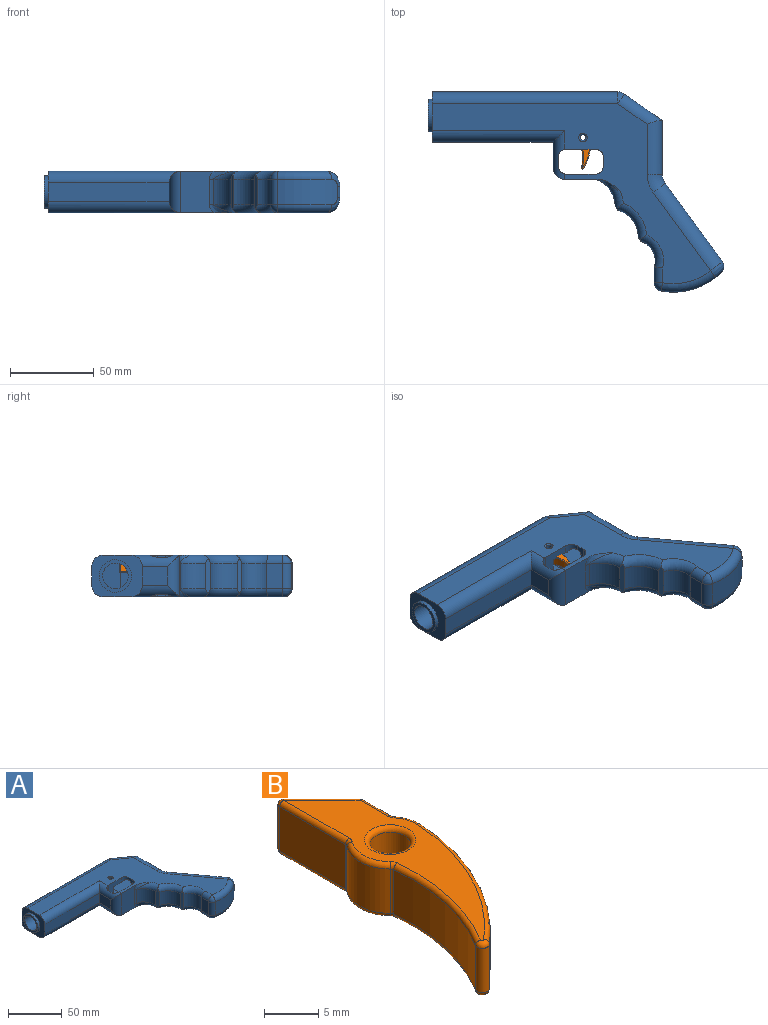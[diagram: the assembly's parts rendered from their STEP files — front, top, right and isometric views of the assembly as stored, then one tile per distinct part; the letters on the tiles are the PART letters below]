
ASSEMBLY  parts=2 mates=1
PART A: 95 faces, bbox 178.8x123.7x40 mm
  f0: plane 15.06x11mm, normal (-1,0,0), area 165.6mm2, adj f72,f87,f88,f89
  f1: cylinder r=5mm len=5mm, axis (0,0,-1), area 29.1mm2, adj f2,f6,f18,f44,f50,f52
  f2: plane 25x17mm, normal (0,-1,0), area 268.3mm2, adj f1,f3,f17,f18,f43,f44,f45,f65
  f3: cylinder r=5mm len=5mm, axis (0,0,-1), area 29.2mm2, adj f2,f6,f17,f45,f51,f53
  f4: cylinder r=40.62mm len=35.92mm, axis (0,0,-1), area 568.7mm2, adj f25,f28,f29,f33,f34,f42
  f5: plane 22.49x5mm, normal (1,0,0), area 112.4mm2, adj f65,f66,f87,f89
  f6: plane 25x5mm, normal (-1,0,0), area 69.7mm2, adj f1,f3,f17,f18,f19,f52,f53,f55
  f7: plane 25.01x19.08mm, normal (0,-1,0), area 427.6mm2, adj f17,f18,f76,f77,f78,f88
  f8: cylinder r=17mm len=15.25mm, axis (0,0,-1), area 292.7mm2, adj f9,f20,f21,f77
  f9: plane 21.32x3.15mm, normal (-0.86,-0.52,0), area 56.6mm2, adj f8,f10,f20,f21,f22,f23
  f10: cylinder r=17mm len=16.26mm, axis (0,0,-1), area 328mm2, adj f9,f11,f22,f23
  f11: plane 21.33x2.99mm, normal (-0.82,-0.57,0), area 56.7mm2, adj f10,f12,f22,f23,f24,f26
  f12: cylinder r=12mm len=15.05mm, axis (0,0,-1), area 282.2mm2, adj f11,f13,f24,f26
  f13: plane 15x9.54mm, normal (-1,0,0), area 143.2mm2, adj f12,f27,f30,f33
  f14: plane 46.5x34.02mm, normal (0.81,0.59,0), area 403.3mm2, adj f25,f35,f38,f41
  f15: plane 32.06x7mm, normal (1,0,0), area 224.4mm2, adj f36,f38,f39,f73
  f16: plane 25x17mm, normal (0,1,0), area 425mm2, adj f17,f18,f19,f66
  f17: plane 165.74x107.32mm, normal (0,0,1), area 4323.9mm2, adj f2,f3,f6,f7,f16,f19,f20,f22
  f18: plane 165.74x107.32mm, normal (0,0,-1), area 4323.9mm2, adj f1,f2,f6,f7,f16,f19,f21,f23
  f19: cylinder r=5mm len=25mm, axis (0,0,1), area 196.3mm2, adj f6,f16,f17,f18
  f20: torus R=22mm, axis (0,0,1), area 115.2mm2, adj f8,f9,f17,f22,f78
  f21: torus R=22mm, axis (0,0,1), area 115.2mm2, adj f8,f9,f18,f23,f76
  f22: torus R=22mm, axis (0,0,1), area 190.9mm2, adj f9,f10,f11,f17,f20,f24
  f23: torus R=22mm, axis (0,0,1), area 190.9mm2, adj f9,f10,f11,f18,f21,f26
  f24: torus R=17mm, axis (0,0,1), area 168mm2, adj f11,f12,f17,f22,f27
  f25: cylinder r=5mm len=7mm, axis (0,0,-1), area 49.6mm2, adj f4,f14,f34,f42
  f26: torus R=17mm, axis (0,0,1), area 168mm2, adj f11,f12,f18,f23,f30
  f27: cylinder r=5mm len=9.54mm, axis (0,1,0), area 72.2mm2, adj f13,f17,f24,f31
  f28: torus R=35.62mm, axis (0,0,1), area 259.2mm2, adj f4,f17,f31,f34
  f29: torus R=35.62mm, axis (0,0,1), area 259.2mm2, adj f4,f18,f32,f42
  f30: cylinder r=5mm len=9.54mm, axis (0,-1,0), area 72.2mm2, adj f13,f18,f26,f32
  f31: sphere r=5mm, area 34.8mm2, adj f27,f28,f33
  f32: sphere r=5mm, area 34.8mm2, adj f29,f30,f33
  f33: cylinder r=5mm len=15mm, axis (0,0,-1), area 104.4mm2, adj f4,f13,f31,f32
  f34: bspline ~10.77x10.52mm, area 85.1mm2, adj f4,f25,f28,f35
  f35: cylinder r=9mm len=52.13mm, axis (0.59,-0.81,0), area 817.3mm2, adj f14,f17,f34,f37
  f36: cylinder r=9mm len=32.06mm, axis (0,-1,0), area 445.2mm2, adj f15,f17,f37,f70,f79
  f37: torus R=18mm, axis (0,0,1), area 109.6mm2, adj f17,f35,f36,f38
  f38: cylinder r=9mm len=7mm, axis (0,0,1), area 39.8mm2, adj f14,f15,f37,f40
  f39: cylinder r=9mm len=32.06mm, axis (0,1,0), area 445.2mm2, adj f15,f18,f40,f71,f82
  f40: torus R=18mm, axis (0,0,1), area 109.6mm2, adj f18,f38,f39,f41
  f41: cylinder r=9mm len=52.13mm, axis (-0.59,0.81,0), area 817.3mm2, adj f14,f18,f40,f42
  f42: bspline ~10.63x10.55mm, area 85.1mm2, adj f4,f25,f29,f41
  f43: plane 15x4mm, normal (1,0,0), area 60mm2, adj f2,f44,f45,f58
  f44: plane 17.55x16.25mm, normal (0,0,1), area 233.8mm2, adj f1,f2,f43,f48,f49,f50,f58,f59
  f45: plane 17.63x16.27mm, normal (0,0,-1), area 235mm2, adj f2,f3,f43,f48,f49,f51,f58,f60
  f46: cylinder r=1.75mm len=3.5mm, axis (0,0,1), area 38.5mm2, adj f63,f64
  f47: cylinder r=1.75mm len=3.5mm, axis (0,0,1), area 38.5mm2, adj f61,f62
  f48: plane 17x12mm, normal (1,0,0), area 133.9mm2, adj f44,f45,f49,f59,f60,f69,f91
  f49: plane 15x4.55mm, normal (0,1,0), area 68.3mm2, adj f44,f45,f48,f58
  f50: plane 18.9x2.42mm, normal (0.71,0,0.71), area 49.9mm2, adj f1,f44,f52,f59,f69
  f51: plane 18.89x2.41mm, normal (0.72,0,-0.69), area 49.1mm2, adj f3,f45,f53,f60,f69
  f52: plane 27.45x23mm, normal (0,0,1), area 626.3mm2, adj f1,f6,f50,f56,f68,f69
  f53: plane 27.45x23mm, normal (0,0,-1), area 626.3mm2, adj f3,f6,f51,f57,f67,f69
  f54: plane 25x15mm, normal (-1,0,0), area 375mm2, adj f55,f56,f57,f69
  f55: plane 28x15mm, normal (0,1,0), area 420mm2, adj f6,f54,f67,f68
  f56: plane 25.84x2.84mm, normal (-0.71,0,0.71), area 69.5mm2, adj f52,f54,f68,f69
  f57: plane 25.84x2.84mm, normal (-0.71,0,-0.71), area 69.5mm2, adj f53,f54,f67,f69
  f58: cylinder r=1mm len=15mm, axis (0,0,-1), area 23.6mm2, adj f43,f44,f45,f49
  f59: cylinder r=1mm len=18.55mm, axis (-1,0,0), area 28.4mm2, adj f44,f48,f50,f69
  f60: cylinder r=1mm len=18.59mm, axis (1,0,0), area 28.4mm2, adj f45,f48,f51,f69
  f61: torus R=2.5mm, axis (0,0,1), area 15mm2, adj f18,f47
  f62: torus R=2.5mm, axis (0,0,1), area 15mm2, adj f44,f47
  f63: torus R=2.5mm, axis (0,0,1), area 15mm2, adj f45,f46
  f64: torus R=2.5mm, axis (0,0,1), area 15mm2, adj f17,f46
  f65: cylinder r=5mm len=25mm, axis (0,0,1), area 187.8mm2, adj f2,f5,f17,f18,f87,f89
  f66: cylinder r=5mm len=25mm, axis (0,0,-1), area 187.8mm2, adj f5,f16,f17,f18,f87,f89
  f67: cylinder r=2mm len=28mm, axis (1,0,0), area 84.8mm2, adj f6,f53,f55,f57
  f68: cylinder r=2mm len=28mm, axis (-1,0,0), area 84.8mm2, adj f6,f52,f55,f56
  f69: plane 49x19mm, normal (0,-1,0), area 622.5mm2, adj f48,f50,f51,f52,f53,f54,f56,f57
  f70: plane 7.31x3.58mm, normal (0,-1,0), area 1.5mm2, adj f36,f73,f79
  f71: plane 7.31x3.58mm, normal (0,-1,0), area 1.5mm2, adj f39,f73,f82
  f72: plane 72.02x11mm, normal (0,-1,0), area 792.2mm2, adj f0,f75,f86,f90
  f73: plane 22.6x15.8mm, normal (0.57,0.82,0), area 303.4mm2, adj f15,f70,f71,f79,f82,f85
  f74: plane 110.4x11mm, normal (0,1,0), area 1214.4mm2, adj f75,f80,f81,f85
  f75: plane 30.01x25mm, normal (-1,0,0), area 415.5mm2, adj f17,f18,f72,f74,f80,f81,f86,f90
  f76: bspline ~17.12x13.36mm, area 42.1mm2, adj f7,f18,f21,f77
  f77: cylinder r=7mm len=15mm, axis (0,0,-1), area 41.8mm2, adj f7,f8,f76,f78
  f78: bspline ~17.12x13.36mm, area 42.1mm2, adj f7,f17,f20,f77
  f79: cylinder r=7mm len=26.61mm, axis (0.82,-0.57,0), area 272.3mm2, adj f17,f36,f70,f73,f83
  f80: cylinder r=7mm len=110.4mm, axis (1,0,0), area 1213.9mm2, adj f17,f74,f75,f83
  f81: cylinder r=7mm len=110.4mm, axis (-1,0,0), area 1213.9mm2, adj f18,f74,f75,f84
  f82: cylinder r=7mm len=26.61mm, axis (-0.82,0.57,0), area 272.3mm2, adj f18,f39,f71,f73,f84
  f83: sphere r=7mm, area 29.9mm2, adj f79,f80,f85
  f84: sphere r=7mm, area 29.9mm2, adj f81,f82,f85
  f85: cylinder r=7mm len=11mm, axis (0,0,1), area 47mm2, adj f73,f74,f83,f84
  f86: cylinder r=7mm len=79.02mm, axis (-1,0,0), area 830.3mm2, adj f17,f72,f75,f87
  f87: cylinder r=7mm len=29.06mm, axis (0,1,0), area 200.4mm2, adj f0,f5,f17,f65,f66,f86,f88
  f88: cylinder r=7mm len=25mm, axis (0,0,-1), area 197.9mm2, adj f0,f7,f87,f89
  f89: cylinder r=7mm len=29.06mm, axis (0,-1,0), area 200.4mm2, adj f0,f5,f18,f65,f66,f88,f90
  f90: cylinder r=7mm len=79.02mm, axis (1,0,0), area 830.3mm2, adj f18,f72,f75,f89
  f91: cylinder r=7.65mm len=102.5mm, axis (-1,0,0), area 4590.6mm2, adj f48,f69,f92,f94
  f92: plane 15.3x10.71mm, normal (-1,0,0), area 137.4mm2, adj f69,f91
  f93: cylinder r=9.65mm len=19.3mm, axis (1,0,0), area 151.6mm2, adj f75,f94
  f94: plane 19.3x19.3mm, normal (-1,0,0), area 108.7mm2, adj f91,f93
PART B: 50 faces, bbox 12x31.3x6 mm
  f0: plane 8.59x5mm, normal (-1,0,0), area 42.9mm2, adj f23,f32,f33,f34
  f1: cylinder r=4mm len=5.37mm, axis (0,0,-1), area 29.5mm2, adj f14,f22,f23,f24
  f2: cylinder r=22mm len=13.85mm, axis (0,0,-1), area 72.4mm2, adj f11,f13,f14,f15
  f3: cylinder r=0.66mm len=5mm, axis (0,0,-1), area 9.9mm2, adj f4,f11,f17,f20
  f4: cylinder r=25mm len=17.72mm, axis (0,0,-1), area 101.7mm2, adj f3,f21,f25,f26
  f5: cylinder r=4mm len=5mm, axis (0,0,-1), area 13.4mm2, adj f26,f31,f35,f36
  f6: plane 5x3.61mm, normal (1,0,0), area 18.1mm2, adj f36,f41,f44,f47
  f7: plane 5x5mm, normal (0.71,0.71,0), area 35.4mm2, adj f33,f42,f43,f47
  f8: cylinder r=1.88mm len=5mm, axis (0,0,-1), area 58.9mm2, adj f48,f49
  f9: plane 28.93x8.97mm, normal (0,0,1), area 94.3mm2, adj f13,f17,f18,f21,f22,f28,f31,f32
  f10: plane 28.93x8.97mm, normal (0,0,-1), area 94.3mm2, adj f15,f19,f20,f24,f25,f29,f34,f35
  f11: cylinder r=0.5mm len=5mm, axis (0,0,1), area 0.2mm2, adj f2,f3,f12,f16
  f12: sphere r=0.5mm, area 0mm2, adj f11,f13,f17
  f13: torus R=22.5mm, axis (0,0,1), area 11.5mm2, adj f2,f9,f12,f18
  f14: cylinder r=0.5mm len=5mm, axis (0,0,-1), area 1.7mm2, adj f1,f2,f18,f19
  f15: torus R=22.5mm, axis (0,0,1), area 11.5mm2, adj f2,f10,f16,f19
  f16: sphere r=0.5mm, area 0mm2, adj f11,f15,f20
  f17: torus R=0.16mm, axis (0,0,1), area 1.1mm2, adj f3,f9,f12,f21
  f18: torus R=1mm, axis (0,0,1), area 0.4mm2, adj f9,f13,f14,f22
  f19: torus R=1mm, axis (0,0,1), area 0.4mm2, adj f10,f14,f15,f24
  f20: torus R=0.16mm, axis (0,0,1), area 1.1mm2, adj f3,f10,f16,f25
  f21: torus R=24.5mm, axis (0,0,1), area 15.9mm2, adj f4,f9,f17,f27
  f22: torus R=3.5mm, axis (0,0,1), area 4.4mm2, adj f1,f9,f18,f28
  f23: cylinder r=0.5mm len=5mm, axis (0,0,-1), area 1.7mm2, adj f0,f1,f28,f29
  f24: torus R=3.5mm, axis (0,0,1), area 4.4mm2, adj f1,f10,f19,f29
  f25: torus R=24.5mm, axis (0,0,1), area 15.9mm2, adj f4,f10,f20,f30
  f26: cylinder r=0.5mm len=5mm, axis (0,0,-1), area 0.1mm2, adj f4,f5,f27,f30
  f27: sphere r=0.5mm, area 0mm2, adj f21,f26,f31
  f28: torus R=1mm, axis (0,0,1), area 0.4mm2, adj f9,f22,f23,f32
  f29: torus R=1mm, axis (0,0,1), area 0.4mm2, adj f10,f23,f24,f34
  f30: sphere r=0.5mm, area 0mm2, adj f25,f26,f35
  f31: torus R=3.5mm, axis (0,0,1), area 2mm2, adj f5,f9,f27,f37
  f32: cylinder r=0.5mm len=8.59mm, axis (0,1,0), area 6.7mm2, adj f0,f9,f28,f38
  f33: cylinder r=0.5mm len=5mm, axis (0,0,-1), area 5.9mm2, adj f0,f7,f38,f39
  f34: cylinder r=0.5mm len=8.59mm, axis (0,-1,0), area 6.7mm2, adj f0,f10,f29,f39
  f35: torus R=3.5mm, axis (0,0,1), area 2mm2, adj f5,f10,f30,f40
  f36: cylinder r=0.5mm len=5mm, axis (0,0,-1), area 1.7mm2, adj f5,f6,f37,f40
  f37: torus R=1mm, axis (0,0,1), area 0.4mm2, adj f9,f31,f36,f41
  f38: sphere r=0.5mm, area 0.6mm2, adj f32,f33,f42
  f39: sphere r=0.5mm, area 0.6mm2, adj f33,f34,f43
  f40: torus R=1mm, axis (0,0,1), area 0.4mm2, adj f10,f35,f36,f44
  f41: cylinder r=0.5mm len=3.61mm, axis (0,-1,0), area 2.8mm2, adj f6,f9,f37,f45
  f42: cylinder r=0.5mm len=5.35mm, axis (0.71,-0.71,0), area 5.6mm2, adj f7,f9,f38,f45
  f43: cylinder r=0.5mm len=5.35mm, axis (-0.71,0.71,0), area 5.6mm2, adj f7,f10,f39,f46
  f44: cylinder r=0.5mm len=3.61mm, axis (0,1,0), area 2.8mm2, adj f6,f10,f40,f46
  f45: sphere r=0.5mm, area 0.2mm2, adj f41,f42,f47
  f46: sphere r=0.5mm, area 0.2mm2, adj f43,f44,f47
  f47: cylinder r=0.5mm len=5mm, axis (0,0,-1), area 2mm2, adj f6,f7,f45,f46
  f48: torus R=2.38mm, axis (0,0,1), area 10.1mm2, adj f8,f10
  f49: torus R=2.38mm, axis (0,0,1), area 10.1mm2, adj f8,f9
PLACE A t=(-5.19,6.81,-9.75)mm fixed
PLACE B rot(axis=(0,0,1),16deg) t=(-53.09,31.4,5)mm
MATE revolute B.f1 <-> A.f62  axis (0,0,1) through (-52.46,31.67,11)mm
